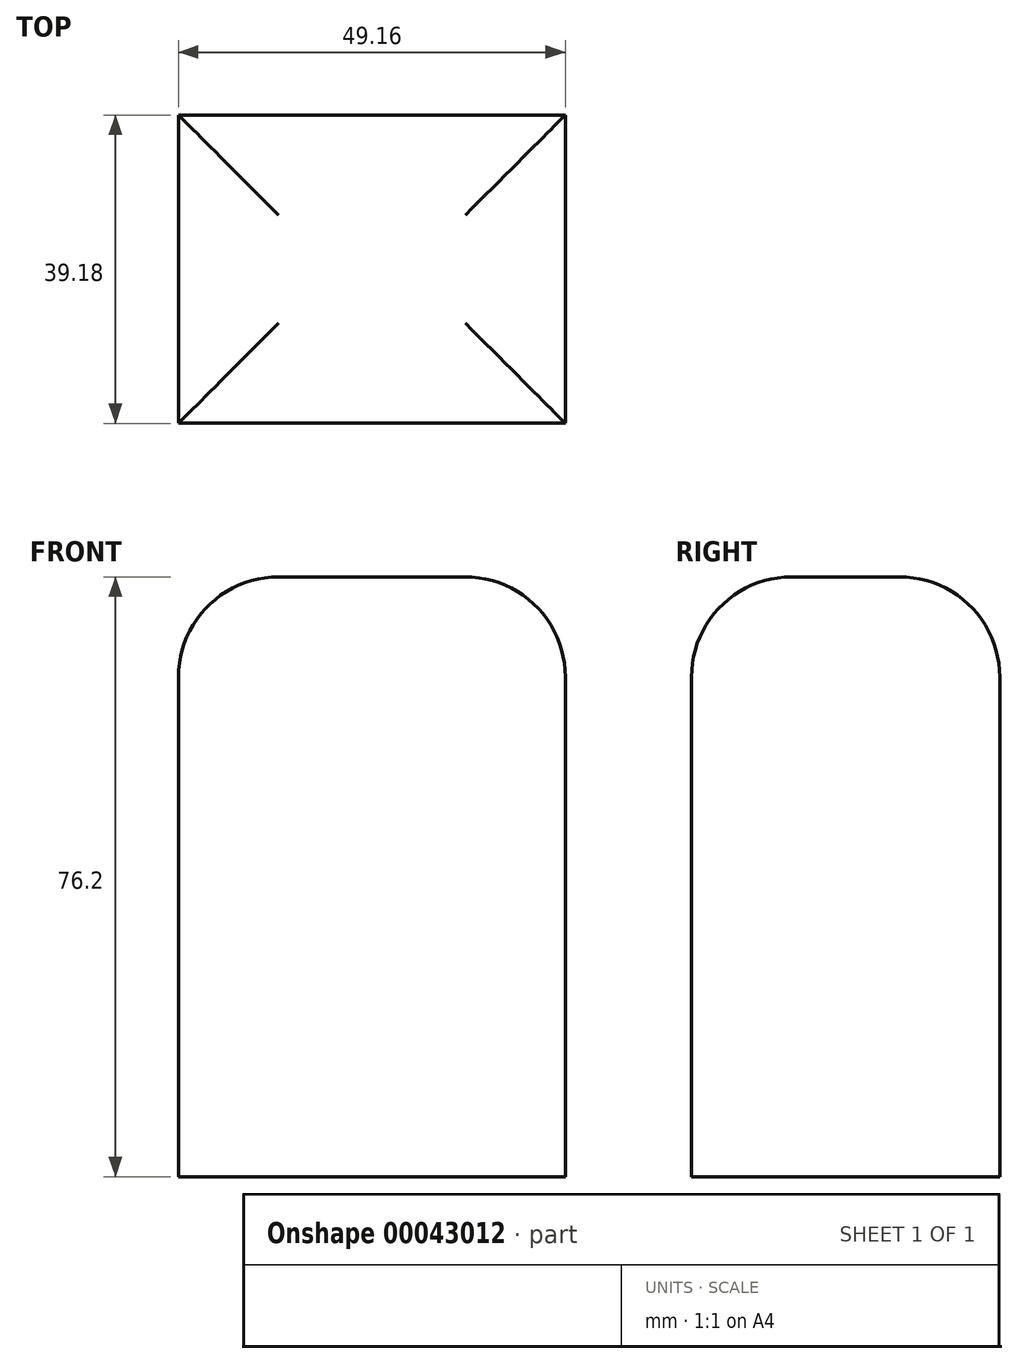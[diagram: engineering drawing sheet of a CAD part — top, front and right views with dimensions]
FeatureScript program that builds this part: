
annotation { "Feature Type Name" : "Feature", "Feature Type Description" : "" }
export const myFeature = defineFeature(function(context is Context, id is Id, definition is map)
    precondition{}
    {
        {
            var Q0;
            Q0=qCreatedBy(makeId("Top.planeOp"),FACE);
            var sketch = newSketch(context, id + "F0", { "sketchPlane" : qUnion([Q0])});
            skLineSegment(sketch, "E0.rect.bottom", {"start": v(24.58, 19.59) * mm, "end": v(-24.58, 19.59) * mm});
            skLineSegment(sketch, "E0.rect.top", {"start": v(24.58, -19.59) * mm, "end": v(-24.58, -19.59) * mm});
            skLineSegment(sketch, "E0.rect.left", {"start": v(24.58, 19.59) * mm, "end": v(24.58, -19.59) * mm});
            skLineSegment(sketch, "E0.rect.right", {"start": v(-24.58, 19.59) * mm, "end": v(-24.58, -19.59) * mm});
            skPoint(sketch, "E0.rect.middle", {"position": v(0, 0) * mm});
            skSolve(sketch);
        }
        {
            var Q0;
            Q0 = qSketchRegion(id + "F0", true);
            extrude(context, id + "F1", {"entities" : qUnion([Q0]), "depth" : 76.2 * mm});
        }
        {
            var Q0;
            Q0=makeQuery(id+"F1.opExtrude","CAP_EDGE",EDGE,{"disambiguationData":[OSD([sQuery(id+"F0.wireOp",EDGE,"E0.rect.top")])],"isStart":false});
            var Q1;
            Q1=makeQuery(id+"F1.opExtrude","CAP_EDGE",EDGE,{"disambiguationData":[OSD([sQuery(id+"F0.wireOp",EDGE,"E0.rect.bottom")])],"isStart":false});
            var Q2;
            Q2=makeQuery(id+"F1.opExtrude","CAP_EDGE",EDGE,{"disambiguationData":[OSD([sQuery(id+"F0.wireOp",EDGE,"E0.rect.left")])],"isStart":false});
            var Q3;
            Q3=makeQuery(id+"F1.opExtrude","CAP_EDGE",EDGE,{"disambiguationData":[OSD([sQuery(id+"F0.wireOp",EDGE,"E0.rect.right")])],"isStart":false});
            fillet(context, id + "F2", {"entities" : qUnion([Q0, Q1, Q2, Q3]), "radius" : 12.7 * mm, "tangentPropagation" : true, "allowEdgeOverflow" : false});
        }
    });
